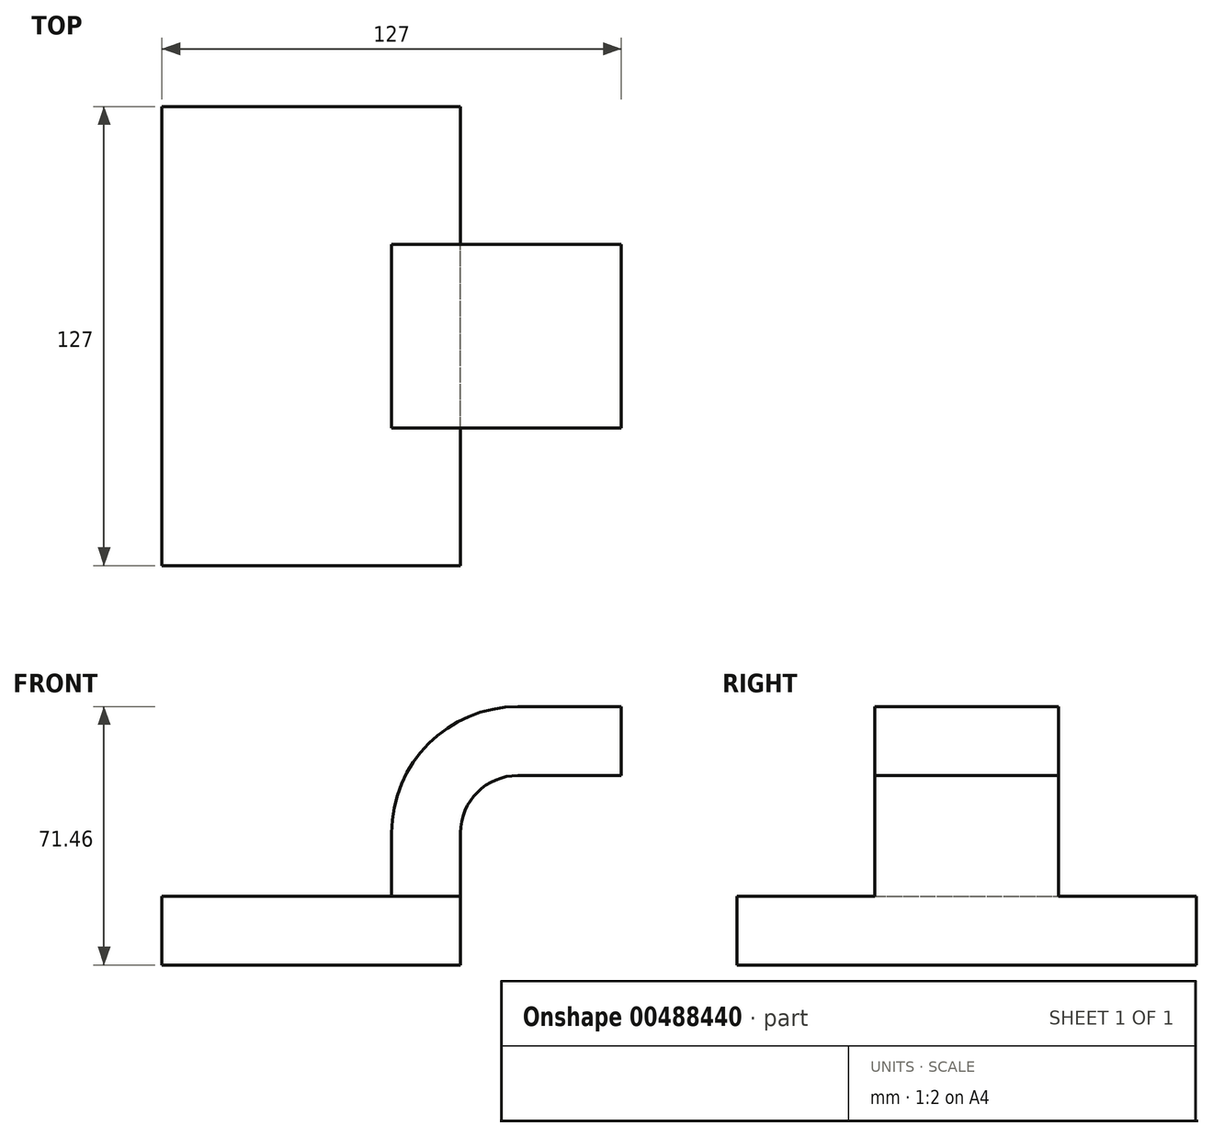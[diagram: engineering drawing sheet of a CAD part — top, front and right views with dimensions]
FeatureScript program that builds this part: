
annotation { "Feature Type Name" : "Feature", "Feature Type Description" : "" }
export const myFeature = defineFeature(function(context is Context, id is Id, definition is map)
    precondition{}
    {
        {
            var Q0;
            Q0=qCreatedBy(makeId("Front.planeOp"),FACE);
            var sketch = newSketch(context, id + "F0", { "sketchPlane" : qUnion([Q0])});
            skLineSegment(sketch, "E0.bottom", {"start": v(41.28, -9.52) * mm, "end": v(-41.28, -9.53) * mm});
            skLineSegment(sketch, "E0.top", {"start": v(41.28, 9.53) * mm, "end": v(-41.28, 9.53) * mm});
            skLineSegment(sketch, "E0.left", {"start": v(41.28, -9.52) * mm, "end": v(41.28, 9.53) * mm});
            skLineSegment(sketch, "E0.right", {"start": v(-41.28, -9.53) * mm, "end": v(-41.28, 9.53) * mm});
            skPoint(sketch, "E0.middle", {"position": v(0, 0) * mm});
            skLineSegment(sketch, "E1.bottom", {"start": v(60.32, 66.68) * mm, "end": v(111.12, 66.68) * mm});
            skLineSegment(sketch, "E1.top", {"start": v(60.33, 38.1) * mm, "end": v(111.12, 38.1) * mm});
            skLineSegment(sketch, "E1.left", {"start": v(60.32, 66.68) * mm, "end": v(60.33, 38.1) * mm});
            skLineSegment(sketch, "E1.right", {"start": v(111.12, 66.68) * mm, "end": v(111.12, 38.1) * mm});
            skPoint(sketch, "E1.middle", {"position": v(85.72, 52.39) * mm});
            skLineSegment(sketch, "E2", {"start": v(41.28, 9.53) * mm, "end": v(41.28, 27) * mm});
            skArc(sketch, "E3", {"start": v(41.27, 27) * mm, "mid": v(45.92, 38.23) * mm, "end": v(57.15, 42.88) * mm});
            skLineSegment(sketch, "E4", {"start": v(57.15, 42.88) * mm, "end": v(85.72, 42.88) * mm});
            skLineSegment(sketch, "E5.0", {"start": v(57.15, 61.93) * mm, "end": v(85.72, 61.93) * mm});
            skArc(sketch, "E5.1", {"start": v(22.23, 27) * mm, "mid": v(32.45, 51.7) * mm, "end": v(57.15, 61.93) * mm});
            skLineSegment(sketch, "E5.2", {"start": v(22.22, 9.53) * mm, "end": v(22.22, 27) * mm});
            skFitSpline(sketch, "E6", {"points": [v(-41.28, 9.53) * mm, v(57.15, 61.93) * mm], "startDerivative": vector(98.43, 52.4) * mm, "endDerivative": vector(136.68, -1.47) * mm});
            skPoint(sketch, "E7.1.internal.snap0", {"position": v(32.45, 51.7) * mm});
            skLineSegment(sketch, "E8", {"start": v(85.72, 38.1) * mm, "end": v(85.72, 66.68) * mm});
            skSolve(sketch);
        }
        {
            var Q0;
            Q0=makeQuery(id+"F0.imprint","IMPRINT",FACE,{"disambiguationData":[TD([[makeQuery(id+"F0.imprint","IMPRINT",EDGE,{"derivedFrom":sQuery(id+"F0.wireOp",EDGE,"E0.bottom")}),-1.0]])]});
            extrude(context, id + "F1", {"entities" : qUnion([Q0]), "endBound" : BoundingType.SYMMETRIC, "depth" : 127 * mm});
        }
        {
            var Q0;
            {var subQ0=sQuery(id+"F0.wireOp",EDGE,"E5.0");var subQ1=sQuery(id+"F0.wireOp",EDGE,"E1.left");var subQ2=makeQuery(id+"F0.imprint","INTERSECT",VERTEX,{"derivedFrom":[subQ1,subQ0]});Q0=makeQuery(id+"F0.imprint","IMPRINT",FACE,{"disambiguationData":[TD([[makeQuery(id+"F0.imprint","IMPRINT",EDGE,{"disambiguationData":[TD([[subQ2,-1.0]])],"derivedFrom":subQ1}),1.0]])]});}
            var Q1;
            {var subQ1=sQuery(id+"F0.wireOp",EDGE,"E2");Q1=makeQuery(id+"F0.imprint","IMPRINT",FACE,{"disambiguationData":[TD([[makeQuery(id+"F0.imprint","IMPRINT",EDGE,{"derivedFrom":subQ1}),1.0]])]});}
            extrude(context, id + "F2", {"entities" : qUnion([Q0, Q1]), "operationType" : NewBodyOperationType.ADD, "endBound" : BoundingType.SYMMETRIC, "depth" : 50.8 * mm});
        }
    });
